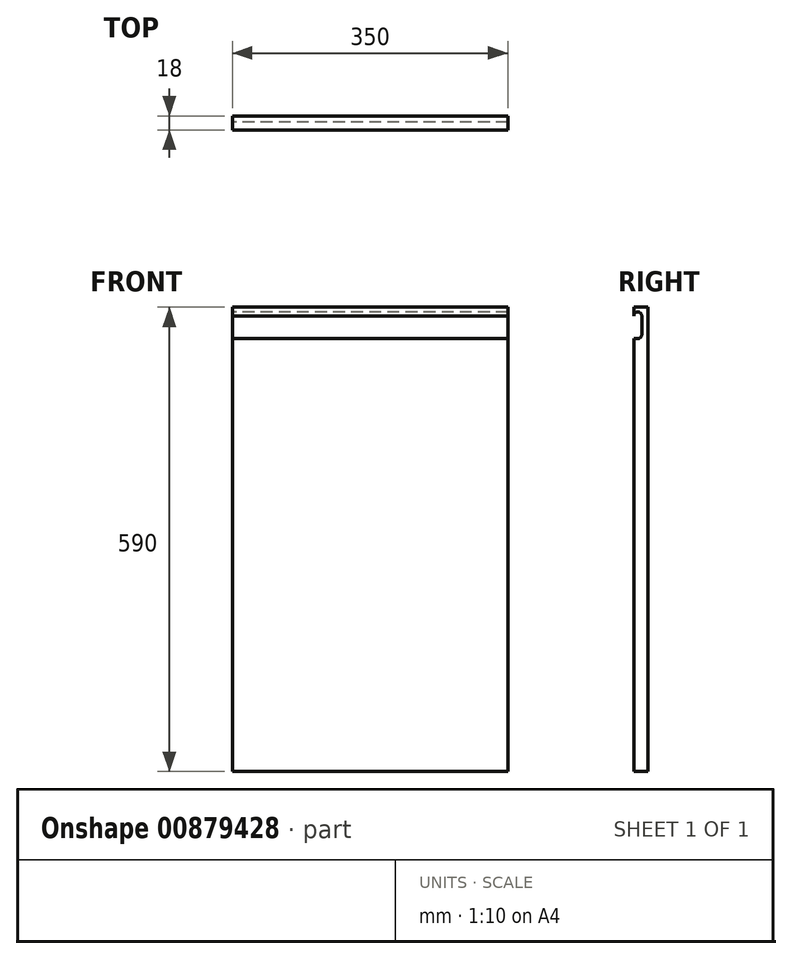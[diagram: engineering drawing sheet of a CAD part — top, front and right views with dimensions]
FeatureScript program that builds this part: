
annotation { "Feature Type Name" : "Feature", "Feature Type Description" : "" }
export const myFeature = defineFeature(function(context is Context, id is Id, definition is map)
    precondition{}
    {
        {
            var Q0;
            Q0=qCreatedBy(makeId("Front.planeOp"),FACE);
            var sketch = newSketch(context, id + "F0", { "sketchPlane" : qUnion([Q0])});
            skLineSegment(sketch, "E0.bottom", {"start": v(0, 0) * mm, "end": v(350, 0) * mm});
            skLineSegment(sketch, "E0.top", {"start": v(0, 590) * mm, "end": v(350, 590) * mm});
            skLineSegment(sketch, "E0.left", {"start": v(0, 0) * mm, "end": v(0, 590) * mm});
            skLineSegment(sketch, "E0.right", {"start": v(350, 0) * mm, "end": v(350, 590) * mm});
            skSolve(sketch);
        }
        {
            var Q0;
            Q0=makeQuery(id+"F0.imprint","IMPRINT",FACE,{"disambiguationData":[TD([[makeQuery(id+"F0.imprint","IMPRINT",EDGE,{"derivedFrom":sQuery(id+"F0.wireOp",EDGE,"E0.bottom")}),1.0]])]});
            extrude(context, id + "F1", {"entities" : qUnion([Q0]), "oppositeDirection" : true, "depth" : 18 * mm, "offsetDistance" : 25 * mm});
        }
        {
            var Q0;
            Q0=makeQuery(id+"F1.opExtrude","SWEPT_FACE",FACE,{"disambiguationData":[OSD([sQuery(id+"F0.wireOp",EDGE,"E0.left")])]});
            var sketch = newSketch(context, id + "F2", { "sketchPlane" : qUnion([Q0])});
            skLineSegment(sketch, "E1", {"start": v(0, 550) * mm, "end": v(-5, 550) * mm});
            skLineSegment(sketch, "E2", {"start": v(-10, 555) * mm, "end": v(-10, 579) * mm});
            skArc(sketch, "E3", {"start": v(0, 579) * mm, "mid": v(-5, 584) * mm, "end": v(-10, 579) * mm});
            skPoint(sketch, "E4.visualSharp", {"position": v(-10, 550) * mm});
            skArc(sketch, "E4.filletArc", {"start": v(-10, 555) * mm, "mid": v(-8.54, 551.46) * mm, "end": v(-5, 550) * mm});
            skSolve(sketch);
        }
        {
            var Q0;
            {var subQ1=sQuery(id+"F2.wireOp",EDGE,"E1");Q0=makeQuery(id+"F2.imprint","IMPRINT",FACE,{"disambiguationData":[TD([[makeQuery(id+"F2.imprint","IMPRINT",EDGE,{"derivedFrom":subQ1}),-1.0]])]});}
            extrude(context, id + "F3", {"entities" : qUnion([Q0]), "operationType" : NewBodyOperationType.REMOVE, "oppositeDirection" : true, "depth" : 452 * mm, "offsetDistance" : 25 * mm});
        }
    });
